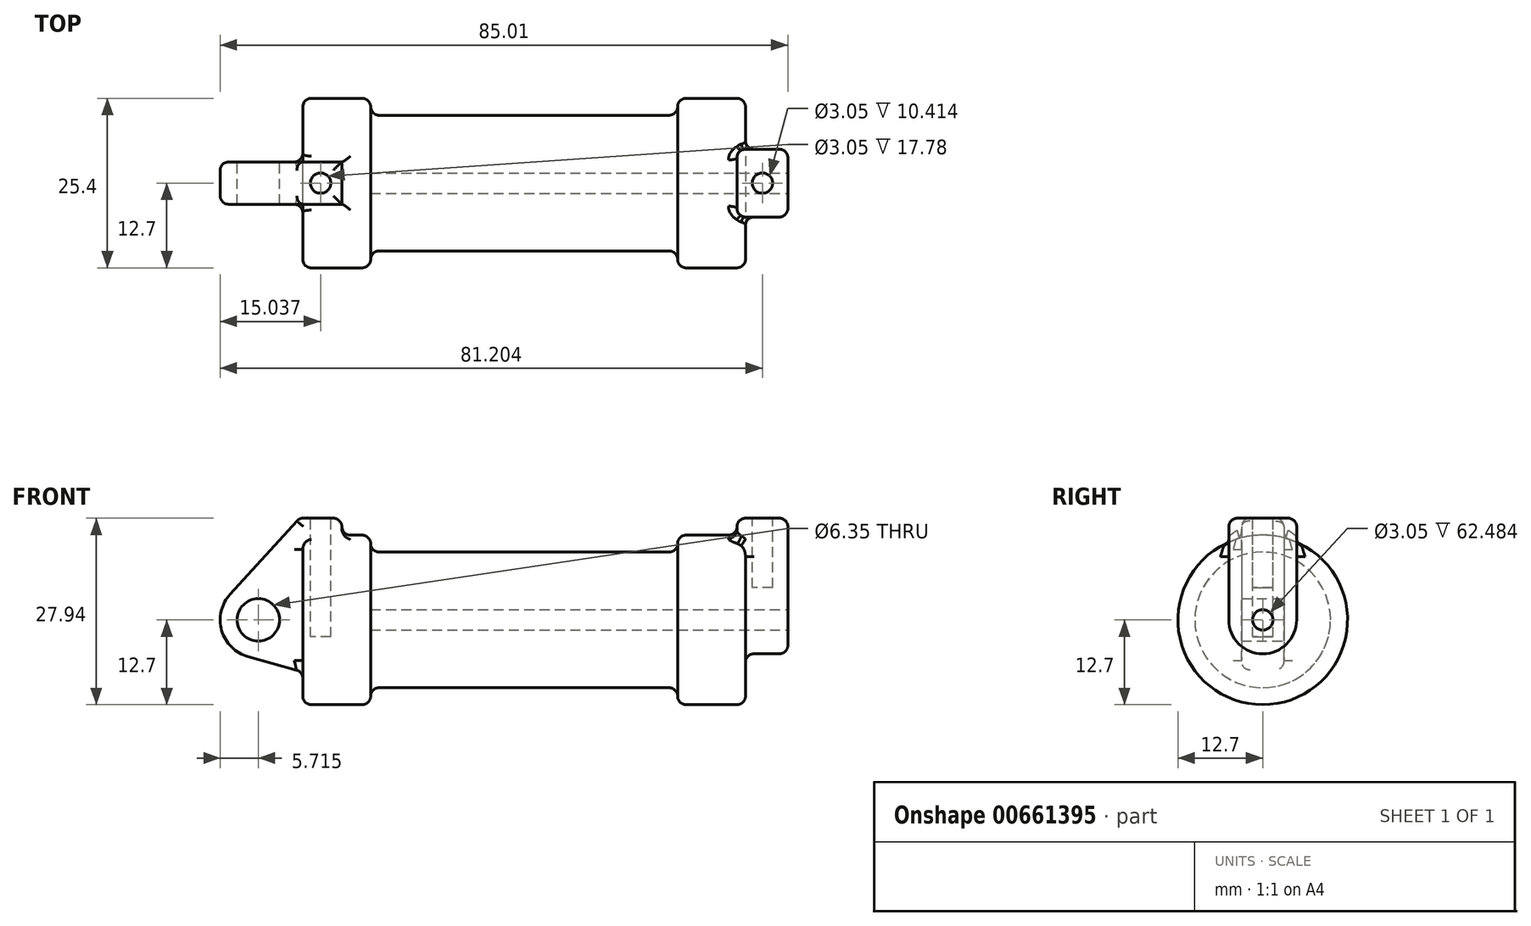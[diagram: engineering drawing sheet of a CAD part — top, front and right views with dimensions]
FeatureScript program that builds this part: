
annotation { "Feature Type Name" : "Feature", "Feature Type Description" : "" }
export const myFeature = defineFeature(function(context is Context, id is Id, definition is map)
    precondition{}
    {
        {
            var Q0;
            Q0=qCreatedBy(makeId("Front.planeOp"),FACE);
            var sketch = newSketch(context, id + "F0", { "sketchPlane" : qUnion([Q0])});
            skLineSegment(sketch, "E0", {"start": v(0, 0) * mm, "end": v(0, 12.7) * mm});
            skLineSegment(sketch, "E1", {"start": v(0, 12.7) * mm, "end": v(10.16, 12.7) * mm});
            skLineSegment(sketch, "E2", {"start": v(10.16, 12.7) * mm, "end": v(10.16, 10.16) * mm});
            skLineSegment(sketch, "E3", {"start": v(10.16, 10.16) * mm, "end": v(56.13, 10.16) * mm});
            skLineSegment(sketch, "E4", {"start": v(56.13, 10.16) * mm, "end": v(56.13, 12.7) * mm});
            skLineSegment(sketch, "E5", {"start": v(56.13, 12.7) * mm, "end": v(66.3, 12.7) * mm});
            skLineSegment(sketch, "E6", {"start": v(66.3, 12.7) * mm, "end": v(66.3, 0) * mm});
            skLineSegment(sketch, "E7", {"start": v(66.3, 0) * mm, "end": v(0, 0) * mm});
            skLineSegment(sketch, "E8", {"start": v(5.84, 15.24) * mm, "end": v(-0.5, 15.24) * mm});
            skLineSegment(sketch, "E9", {"start": v(-0.5, 15.24) * mm, "end": v(-10.88, 3.85) * mm});
            skLineSegment(sketch, "E10", {"start": v(0, 0) * mm, "end": v(-6.65, 0) * mm});
            skCircle(sketch, "E11", {"center": v(-6.65, 0) * mm, "radius": 5.72 * mm});
            skCircle(sketch, "E12", {"center": v(-6.65, 0) * mm, "radius": 3.18 * mm});
            skLineSegment(sketch, "E13", {"start": v(5.84, 15.24) * mm, "end": v(5.84, -9.4) * mm});
            skLineSegment(sketch, "E14", {"start": v(5.84, -9.4) * mm, "end": v(-8.18, -5.5) * mm});
            skSolve(sketch);
        }
        {
            var Q0;
            {var subQ1=sQuery(id+"F0.wireOp",EDGE,"E0");Q0=makeQuery(id+"F0.imprint","IMPRINT",FACE,{"disambiguationData":[TD([[makeQuery(id+"F0.imprint","IMPRINT",EDGE,{"derivedFrom":subQ1}),1.0]])]});}
            var Q1;
            {var subQ0=sQuery(id+"F0.wireOp",EDGE,"E14");Q1=makeQuery(id+"F0.imprint","IMPRINT",FACE,{"disambiguationData":[TD([[makeQuery(id+"F0.imprint","IMPRINT",EDGE,{"derivedFrom":subQ0}),-1.0]])]});}
            var Q2;
            {var subQ5=sQuery(id+"F0.wireOp",EDGE,"E12");Q2=makeQuery(id+"F0.imprint","IMPRINT",FACE,{"disambiguationData":[TD([[makeQuery(id+"F0.imprint","IMPRINT",EDGE,{"derivedFrom":subQ5}),-1.0]])]});}
            extrude(context, id + "F1", {"entities" : qUnion([Q0, Q1, Q2]), "endBound" : BoundingType.SYMMETRIC, "depth" : 6.35 * mm, "offsetDistance" : 25.4 * mm});
        }
        {
            var Q0;
            {var subQ0=sQuery(id+"F0.wireOp",EDGE,"E0");Q0=makeQuery(id+"F0.imprint","IMPRINT",FACE,{"disambiguationData":[TD([[makeQuery(id+"F0.imprint","IMPRINT",EDGE,{"derivedFrom":subQ0}),-1.0]])]});}
            var Q1;
            {var subQ0=sQuery(id+"F0.wireOp",EDGE,"E2");Q1=makeQuery(id+"F0.imprint","IMPRINT",FACE,{"disambiguationData":[TD([[makeQuery(id+"F0.imprint","IMPRINT",EDGE,{"derivedFrom":subQ0}),-1.0]])]});}
            var Q2;
            Q2=sQuery(id+"F0.wireOp",EDGE,"E7");
            revolve(context, id + "F2", {"operationType" : NewBodyOperationType.INTERSECT, "entities" : qUnion([Q0, Q1]), "axis" : qUnion([Q2]), "revolveType" : RevolveType.FULL});
        }
        {
            var Q0;
            Q0=makeQuery(id+"F1.opExtrude","SWEPT_BODY",BODY,{"disambiguationData":[OSD([sQuery(id+"F0.wireOp",EDGE,"E0"),sQuery(id+"F0.wireOp",EDGE,"E1"),sQuery(id+"F0.wireOp",EDGE,"E7"),sQuery(id+"F0.wireOp",EDGE,"E8"),sQuery(id+"F0.wireOp",EDGE,"E9"),sQuery(id+"F0.wireOp",EDGE,"E11"),sQuery(id+"F0.wireOp",EDGE,"E12"),sQuery(id+"F0.wireOp",EDGE,"E13"),sQuery(id+"F0.wireOp",EDGE,"E14")])]});
            deleteBodies(context, id + "F3", {"entities" : qUnion([Q0])});
        }
        {
            var Q0;
            {var subQ0=sQuery(id+"F0.wireOp",EDGE,"E2");Q0=makeQuery(id+"F0.imprint","IMPRINT",FACE,{"disambiguationData":[TD([[makeQuery(id+"F0.imprint","IMPRINT",EDGE,{"derivedFrom":subQ0}),-1.0]])]});}
            var Q1;
            {var subQ0=sQuery(id+"F0.wireOp",EDGE,"E0");Q1=makeQuery(id+"F0.imprint","IMPRINT",FACE,{"disambiguationData":[TD([[makeQuery(id+"F0.imprint","IMPRINT",EDGE,{"derivedFrom":subQ0}),-1.0]])]});}
            var Q2;
            Q2=sQuery(id+"F0.wireOp",EDGE,"E7");
            revolve(context, id + "F4", {"entities" : qUnion([Q0, Q1]), "axis" : qUnion([Q2]), "revolveType" : RevolveType.FULL});
        }
        {
            var Q0;
            {var subQ0=sQuery(id+"F0.wireOp",EDGE,"E0");Q0=makeQuery(id+"F0.imprint","IMPRINT",FACE,{"disambiguationData":[TD([[makeQuery(id+"F0.imprint","IMPRINT",EDGE,{"derivedFrom":subQ0}),-1.0]])]});}
            var Q1;
            {var subQ0=sQuery(id+"F0.wireOp",EDGE,"E14");Q1=makeQuery(id+"F0.imprint","IMPRINT",FACE,{"disambiguationData":[TD([[makeQuery(id+"F0.imprint","IMPRINT",EDGE,{"derivedFrom":subQ0}),-1.0]])]});}
            var Q2;
            {var subQ5=sQuery(id+"F0.wireOp",EDGE,"E12");Q2=makeQuery(id+"F0.imprint","IMPRINT",FACE,{"disambiguationData":[TD([[makeQuery(id+"F0.imprint","IMPRINT",EDGE,{"derivedFrom":subQ5}),-1.0]])]});}
            var Q3;
            {var subQ1=sQuery(id+"F0.wireOp",EDGE,"E0");Q3=makeQuery(id+"F0.imprint","IMPRINT",FACE,{"disambiguationData":[TD([[makeQuery(id+"F0.imprint","IMPRINT",EDGE,{"derivedFrom":subQ1}),1.0]])]});}
            extrude(context, id + "F5", {"entities" : qUnion([Q0, Q1, Q2, Q3]), "operationType" : NewBodyOperationType.ADD, "endBound" : BoundingType.SYMMETRIC, "depth" : 6.35 * mm, "offsetDistance" : 25.4 * mm});
        }
        {
            var Q0;
            Q0=makeQuery(id+"F4.opRevolve","SWEPT_FACE",FACE,{"disambiguationData":[OSD([sQuery(id+"F0.wireOp",EDGE,"E6")])]});
            var sketch = newSketch(context, id + "F6", { "sketchPlane" : qUnion([Q0])});
            skCircle(sketch, "E15", {"center": v(0, 0) * mm, "radius": 1.52 * mm});
            skCircle(sketch, "E16", {"center": v(0, 0) * mm, "radius": 5.08 * mm});
            skLineSegment(sketch, "E17", {"start": v(5.08, 0) * mm, "end": v(5.08, 15.24) * mm});
            skLineSegment(sketch, "E18", {"start": v(-5.08, 0) * mm, "end": v(-5.08, 15.24) * mm});
            skLineSegment(sketch, "E19", {"start": v(-5.08, 15.24) * mm, "end": v(5.08, 15.24) * mm});
            skSolve(sketch);
        }
        {
            var Q0;
            {var subQ0=sQuery(id+"F6.wireOp",EDGE,"E19");Q0=makeQuery(id+"F6.imprint","IMPRINT",FACE,{"disambiguationData":[TD([[makeQuery(id+"F6.imprint","IMPRINT",EDGE,{"derivedFrom":subQ0}),-1.0]])]});}
            var Q1;
            {var subQ0=sQuery(id+"F6.wireOp",EDGE,"E17");var subQ1=sQuery(id+"F6.wireOp",EDGE,"E16");var subQ2=makeQuery(id+"F6.imprint","INTERSECT",VERTEX,{"derivedFrom":[subQ1,subQ0]});Q1=makeQuery(id+"F6.imprint","IMPRINT",FACE,{"disambiguationData":[TD([[makeQuery(id+"F6.imprint","IMPRINT",EDGE,{"disambiguationData":[TD([[subQ2,-1.0]])],"derivedFrom":subQ1}),-1.0]])]});}
            var Q2;
            Q2=makeQuery(id+"F6.imprint","IMPRINT",FACE,{"disambiguationData":[TD([[makeQuery(id+"F6.imprint","IMPRINT",EDGE,{"derivedFrom":sQuery(id+"F6.wireOp",EDGE,"E15")}),-1.0]])]});
            extrude(context, id + "F7", {"entities" : qUnion([Q0, Q1, Q2]), "operationType" : NewBodyOperationType.ADD, "oppositeDirection" : true, "depth" : 1.27 * mm, "offsetDistance" : 25.4 * mm, "hasSecondDirection" : true, "secondDirectionOppositeDirection" : false, "secondDirectionDepth" : 6.35 * mm});
        }
        {
            var Q0;
            Q0=makeQuery(id+"F7.boolean.opBoolean","SPLIT",FACE,{"disambiguationData":[TD([makeQuery(id+"F7.opExtrude","SWEPT_FACE",FACE,{"disambiguationData":[OSD([sQuery(id+"F6.wireOp",EDGE,"E15")])]})])],"derivedFrom":makeQuery(id+"F4.opRevolve","SWEPT_FACE",FACE,{"disambiguationData":[OSD([sQuery(id+"F0.wireOp",EDGE,"E6")])]})});
            var Q1;
            Q1=makeQuery(id+"F4.opRevolve","SWEPT_FACE",FACE,{"disambiguationData":[OSD([sQuery(id+"F0.wireOp",EDGE,"E2")])]});
            extrude(context, id + "F8", {"entities" : qUnion([Q0]), "operationType" : NewBodyOperationType.REMOVE, "endBound" : BoundingType.UP_TO_SURFACE, "oppositeDirection" : true, "depth" : 25.4 * mm, "endBoundEntityFace" : qUnion([Q1]), "offsetDistance" : 25.4 * mm});
        }
        {
            var Q0;
            Q0=makeQuery(id+"F7.opExtrude","SWEPT_FACE",FACE,{"disambiguationData":[OSD([sQuery(id+"F6.wireOp",EDGE,"E19")])]});
            var sketch = newSketch(context, id + "F9", { "sketchPlane" : qUnion([Q0])});
            skCircle(sketch, "E20", {"center": v(68.83, 0) * mm, "radius": 1.52 * mm});
            skPoint(sketch, "E20.centerSnap0", {"position": v(68.83, 5.08) * mm});
            skPoint(sketch, "E20.centerSnap1", {"position": v(72.64, 0) * mm});
            skSolve(sketch);
        }
        {
            var Q0;
            Q0=makeQuery(id+"F9.imprint","IMPRINT",FACE,{"disambiguationData":[TD([[makeQuery(id+"F9.imprint","IMPRINT",EDGE,{"derivedFrom":sQuery(id+"F9.wireOp",EDGE,"E20")}),1.0]])]});
            extrude(context, id + "F10", {"entities" : qUnion([Q0]), "operationType" : NewBodyOperationType.REMOVE, "oppositeDirection" : true, "depth" : 10.4 * mm, "offsetDistance" : 25.4 * mm});
        }
        {
            var Q0;
            Q0=makeQuery(id+"F5.opExtrude","SWEPT_FACE",FACE,{"disambiguationData":[OSD([sQuery(id+"F0.wireOp",EDGE,"E8")])]});
            var sketch = newSketch(context, id + "F11", { "sketchPlane" : qUnion([Q0])});
            skCircle(sketch, "E21", {"center": v(2.67, 0) * mm, "radius": 1.52 * mm});
            skPoint(sketch, "E21.centerSnap0", {"position": v(5.84, 0) * mm});
            skPoint(sketch, "E21.centerSnap1", {"position": v(2.67, 3.18) * mm});
            skSolve(sketch);
        }
        {
            var Q0;
            Q0=makeQuery(id+"F11.imprint","IMPRINT",FACE,{"disambiguationData":[TD([[makeQuery(id+"F11.imprint","IMPRINT",EDGE,{"derivedFrom":sQuery(id+"F11.wireOp",EDGE,"E21")}),1.0]])]});
            extrude(context, id + "F12", {"entities" : qUnion([Q0]), "operationType" : NewBodyOperationType.REMOVE, "oppositeDirection" : true, "depth" : 17.78 * mm, "offsetDistance" : 25.4 * mm});
        }
        {
            var Q0;
            Q0=makeQuery(id+"F4.opRevolve","SWEPT_EDGE",EDGE,{"disambiguationData":[OSD([sQuery(id+"F0.wireOp",EDGE,"E0"),sQuery(id+"F0.wireOp",EDGE,"E1")])]});
            var Q1;
            Q1=makeQuery(id+"F4.opRevolve","SWEPT_EDGE",EDGE,{"disambiguationData":[OSD([sQuery(id+"F0.wireOp",EDGE,"E1"),sQuery(id+"F0.wireOp",EDGE,"E2")])]});
            var Q2;
            Q2=makeQuery(id+"F4.opRevolve","SWEPT_EDGE",EDGE,{"disambiguationData":[OSD([sQuery(id+"F0.wireOp",EDGE,"E4"),sQuery(id+"F0.wireOp",EDGE,"E5")])]});
            var Q3;
            Q3=makeQuery(id+"F4.opRevolve","SWEPT_EDGE",EDGE,{"disambiguationData":[OSD([sQuery(id+"F0.wireOp",EDGE,"E5"),sQuery(id+"F0.wireOp",EDGE,"E6")])]});
            fillet(context, id + "F13", {"entities" : qUnion([Q0, Q1, Q2, Q3]), "radius" : 1.27 * mm, "tangentPropagation" : true, "allowEdgeOverflow" : false});
        }
        {
            var Q0;
            Q0=makeQuery(id+"F7.opExtrude","CAP_EDGE",EDGE,{"disambiguationData":[OSD([sQuery(id+"F6.wireOp",EDGE,"E17")])],"isStart":true});
            var Q1;
            Q1=makeQuery(id+"F7.opExtrude","CAP_EDGE",EDGE,{"disambiguationData":[OSD([sQuery(id+"F6.wireOp",EDGE,"E19")])],"isStart":true});
            var Q2;
            Q2=makeQuery(id+"F7.opExtrude","SWEPT_EDGE",EDGE,{"disambiguationData":[OSD([sQuery(id+"F6.wireOp",EDGE,"E18"),sQuery(id+"F6.wireOp",EDGE,"E19")])]});
            var Q3;
            Q3=makeQuery(id+"F7.opExtrude","CAP_EDGE",EDGE,{"disambiguationData":[OSD([sQuery(id+"F6.wireOp",EDGE,"E19")])],"isStart":false});
            var Q4;
            Q4=makeQuery(id+"F7.opExtrude","SWEPT_EDGE",EDGE,{"disambiguationData":[OSD([sQuery(id+"F6.wireOp",EDGE,"E17"),sQuery(id+"F6.wireOp",EDGE,"E19")])]});
            var Q5;
            Q5=makeQuery(id+"F7.opExtrude","CAP_EDGE",EDGE,{"disambiguationData":[OSD([sQuery(id+"F6.wireOp",EDGE,"E17")])],"isStart":false});
            var Q6;
            Q6=makeQuery(id+"F13.opFillet","BLEND_EDGE",EDGE,{"blendedFrom":[makeQuery(id+"F4.opRevolve","SWEPT_EDGE",EDGE,{"disambiguationData":[OSD([sQuery(id+"F0.wireOp",EDGE,"E5"),sQuery(id+"F0.wireOp",EDGE,"E6")])]}),makeQuery(id+"F7.opExtrude","SWEPT_FACE",FACE,{"disambiguationData":[OSD([sQuery(id+"F6.wireOp",EDGE,"E17")])]})],"blendedInto":[makeQuery(id+"F7.opExtrude","SWEPT_FACE",FACE,{"disambiguationData":[OSD([sQuery(id+"F6.wireOp",EDGE,"E17")])]})]});
            var Q7;
            Q7=makeQuery(id+"F7.boolean.opBoolean","INTERSECT",EDGE,{"derivedFrom":[makeQuery(id+"F4.opRevolve","SWEPT_FACE",FACE,{"disambiguationData":[OSD([sQuery(id+"F0.wireOp",EDGE,"E6")])]}),makeQuery(id+"F7.opExtrude","SWEPT_FACE",FACE,{"disambiguationData":[OSD([sQuery(id+"F6.wireOp",EDGE,"E17")])]})]});
            var Q8;
            Q8=makeQuery(id+"F7.opExtrude","CAP_EDGE",EDGE,{"disambiguationData":[OSD([sQuery(id+"F6.wireOp",EDGE,"E16")])],"isStart":true});
            var Q9;
            Q9=makeQuery(id+"F7.opExtrude","CAP_EDGE",EDGE,{"disambiguationData":[OSD([sQuery(id+"F6.wireOp",EDGE,"E18")])],"isStart":true});
            var Q10;
            Q10=makeQuery(id+"F7.boolean.opBoolean","INTERSECT",EDGE,{"derivedFrom":[makeQuery(id+"F4.opRevolve","SWEPT_FACE",FACE,{"disambiguationData":[OSD([sQuery(id+"F0.wireOp",EDGE,"E6")])]}),makeQuery(id+"F7.opExtrude","SWEPT_FACE",FACE,{"disambiguationData":[OSD([sQuery(id+"F6.wireOp",EDGE,"E16")])]})]});
            var Q11;
            Q11=makeQuery(id+"F7.boolean.opBoolean","INTERSECT",EDGE,{"derivedFrom":[makeQuery(id+"F4.opRevolve","SWEPT_FACE",FACE,{"disambiguationData":[OSD([sQuery(id+"F0.wireOp",EDGE,"E6")])]}),makeQuery(id+"F7.opExtrude","SWEPT_FACE",FACE,{"disambiguationData":[OSD([sQuery(id+"F6.wireOp",EDGE,"E18")])]})]});
            var Q12;
            Q12=makeQuery(id+"F13.opFillet","BLEND_EDGE",EDGE,{"blendedFrom":[makeQuery(id+"F4.opRevolve","SWEPT_EDGE",EDGE,{"disambiguationData":[OSD([sQuery(id+"F0.wireOp",EDGE,"E5"),sQuery(id+"F0.wireOp",EDGE,"E6")])]}),makeQuery(id+"F7.opExtrude","SWEPT_FACE",FACE,{"disambiguationData":[OSD([sQuery(id+"F6.wireOp",EDGE,"E18")])]})],"blendedInto":[makeQuery(id+"F7.opExtrude","SWEPT_FACE",FACE,{"disambiguationData":[OSD([sQuery(id+"F6.wireOp",EDGE,"E18")])]})]});
            var Q13;
            Q13=makeQuery(id+"F7.opExtrude","CAP_EDGE",EDGE,{"disambiguationData":[OSD([sQuery(id+"F6.wireOp",EDGE,"E18")])],"isStart":false});
            var Q14;
            Q14=makeQuery(id+"F7.boolean.opBoolean","INTERSECT",EDGE,{"derivedFrom":[makeQuery(id+"F4.opRevolve","SWEPT_FACE",FACE,{"disambiguationData":[OSD([sQuery(id+"F0.wireOp",EDGE,"E5")])]}),makeQuery(id+"F7.opExtrude","CAP_FACE",FACE,{"disambiguationData":[OSD([sQuery(id+"F6.wireOp",EDGE,"E15"),sQuery(id+"F6.wireOp",EDGE,"E16"),sQuery(id+"F6.wireOp",EDGE,"E17"),sQuery(id+"F6.wireOp",EDGE,"E18"),sQuery(id+"F6.wireOp",EDGE,"E19")])],"isStart":false})]});
            fillet(context, id + "F14", {"entities" : qUnion([Q0, Q1, Q2, Q3, Q4, Q5, Q6, Q7, Q8, Q9, Q10, Q11, Q12, Q13, Q14]), "radius" : 1.27 * mm, "tangentPropagation" : true, "allowEdgeOverflow" : false});
        }
        {
            var Q0;
            Q0=makeQuery(id+"F5.opExtrude","CAP_EDGE",EDGE,{"disambiguationData":[OSD([sQuery(id+"F0.wireOp",EDGE,"E8")])],"isStart":false});
            var Q1;
            Q1=makeQuery(id+"F5.opExtrude","SWEPT_EDGE",EDGE,{"disambiguationData":[OSD([sQuery(id+"F0.wireOp",EDGE,"E8"),sQuery(id+"F0.wireOp",EDGE,"E13")])]});
            var Q2;
            Q2=makeQuery(id+"F5.opExtrude","CAP_EDGE",EDGE,{"disambiguationData":[OSD([sQuery(id+"F0.wireOp",EDGE,"E8")])],"isStart":true});
            var Q3;
            Q3=makeQuery(id+"F5.boolean.opBoolean","INTERSECT",EDGE,{"derivedFrom":[makeQuery(id+"F4.opRevolve","SWEPT_FACE",FACE,{"disambiguationData":[OSD([sQuery(id+"F0.wireOp",EDGE,"E1")])]}),makeQuery(id+"F5.opExtrude","SWEPT_FACE",FACE,{"disambiguationData":[OSD([sQuery(id+"F0.wireOp",EDGE,"E13")])]})]});
            var Q4;
            Q4=makeQuery(id+"F5.boolean.opBoolean","INTERSECT",EDGE,{"derivedFrom":[makeQuery(id+"F4.opRevolve","SWEPT_FACE",FACE,{"disambiguationData":[OSD([sQuery(id+"F0.wireOp",EDGE,"E1")])]}),makeQuery(id+"F5.opExtrude","CAP_FACE",FACE,{"disambiguationData":[OSD([sQuery(id+"F0.wireOp",EDGE,"E8"),sQuery(id+"F0.wireOp",EDGE,"E9"),sQuery(id+"F0.wireOp",EDGE,"E11"),sQuery(id+"F0.wireOp",EDGE,"E12"),sQuery(id+"F0.wireOp",EDGE,"E13"),sQuery(id+"F0.wireOp",EDGE,"E14")])],"isStart":false})]});
            var Q5;
            Q5=makeQuery(id+"F5.boolean.opBoolean","INTERSECT",EDGE,{"derivedFrom":[makeQuery(id+"F4.opRevolve","SWEPT_FACE",FACE,{"disambiguationData":[OSD([sQuery(id+"F0.wireOp",EDGE,"E1")])]}),makeQuery(id+"F5.opExtrude","CAP_FACE",FACE,{"disambiguationData":[OSD([sQuery(id+"F0.wireOp",EDGE,"E8"),sQuery(id+"F0.wireOp",EDGE,"E9"),sQuery(id+"F0.wireOp",EDGE,"E11"),sQuery(id+"F0.wireOp",EDGE,"E12"),sQuery(id+"F0.wireOp",EDGE,"E13"),sQuery(id+"F0.wireOp",EDGE,"E14")])],"isStart":true})]});
            var Q6;
            Q6=makeQuery(id+"F13.opFillet","BLEND_EDGE",EDGE,{"blendedFrom":[makeQuery(id+"F4.opRevolve","SWEPT_EDGE",EDGE,{"disambiguationData":[OSD([sQuery(id+"F0.wireOp",EDGE,"E0"),sQuery(id+"F0.wireOp",EDGE,"E1")])]}),makeQuery(id+"F5.opExtrude","CAP_FACE",FACE,{"disambiguationData":[OSD([sQuery(id+"F0.wireOp",EDGE,"E8"),sQuery(id+"F0.wireOp",EDGE,"E9"),sQuery(id+"F0.wireOp",EDGE,"E11"),sQuery(id+"F0.wireOp",EDGE,"E12"),sQuery(id+"F0.wireOp",EDGE,"E13"),sQuery(id+"F0.wireOp",EDGE,"E14")])],"isStart":true})],"blendedInto":[makeQuery(id+"F5.opExtrude","CAP_FACE",FACE,{"disambiguationData":[OSD([sQuery(id+"F0.wireOp",EDGE,"E8"),sQuery(id+"F0.wireOp",EDGE,"E9"),sQuery(id+"F0.wireOp",EDGE,"E11"),sQuery(id+"F0.wireOp",EDGE,"E12"),sQuery(id+"F0.wireOp",EDGE,"E13"),sQuery(id+"F0.wireOp",EDGE,"E14")])],"isStart":true})]});
            var Q7;
            Q7=makeQuery(id+"F5.boolean.opBoolean","INTERSECT",EDGE,{"derivedFrom":[makeQuery(id+"F4.opRevolve","SWEPT_FACE",FACE,{"disambiguationData":[OSD([sQuery(id+"F0.wireOp",EDGE,"E0")])]}),makeQuery(id+"F5.opExtrude","CAP_FACE",FACE,{"disambiguationData":[OSD([sQuery(id+"F0.wireOp",EDGE,"E8"),sQuery(id+"F0.wireOp",EDGE,"E9"),sQuery(id+"F0.wireOp",EDGE,"E11"),sQuery(id+"F0.wireOp",EDGE,"E12"),sQuery(id+"F0.wireOp",EDGE,"E13"),sQuery(id+"F0.wireOp",EDGE,"E14")])],"isStart":true})]});
            var Q8;
            Q8=makeQuery(id+"F5.opExtrude","CAP_EDGE",EDGE,{"disambiguationData":[OSD([sQuery(id+"F0.wireOp",EDGE,"E9")])],"isStart":true});
            var Q9;
            Q9=makeQuery(id+"F5.opExtrude","CAP_EDGE",EDGE,{"disambiguationData":[OSD([sQuery(id+"F0.wireOp",EDGE,"E9")])],"isStart":false});
            var Q10;
            Q10=makeQuery(id+"F13.opFillet","BLEND_EDGE",EDGE,{"blendedFrom":[makeQuery(id+"F4.opRevolve","SWEPT_EDGE",EDGE,{"disambiguationData":[OSD([sQuery(id+"F0.wireOp",EDGE,"E0"),sQuery(id+"F0.wireOp",EDGE,"E1")])]}),makeQuery(id+"F5.opExtrude","CAP_FACE",FACE,{"disambiguationData":[OSD([sQuery(id+"F0.wireOp",EDGE,"E8"),sQuery(id+"F0.wireOp",EDGE,"E9"),sQuery(id+"F0.wireOp",EDGE,"E11"),sQuery(id+"F0.wireOp",EDGE,"E12"),sQuery(id+"F0.wireOp",EDGE,"E13"),sQuery(id+"F0.wireOp",EDGE,"E14")])],"isStart":false})],"blendedInto":[makeQuery(id+"F5.opExtrude","CAP_FACE",FACE,{"disambiguationData":[OSD([sQuery(id+"F0.wireOp",EDGE,"E8"),sQuery(id+"F0.wireOp",EDGE,"E9"),sQuery(id+"F0.wireOp",EDGE,"E11"),sQuery(id+"F0.wireOp",EDGE,"E12"),sQuery(id+"F0.wireOp",EDGE,"E13"),sQuery(id+"F0.wireOp",EDGE,"E14")])],"isStart":false})]});
            var Q11;
            Q11=makeQuery(id+"F5.boolean.opBoolean","INTERSECT",EDGE,{"derivedFrom":[makeQuery(id+"F4.opRevolve","SWEPT_FACE",FACE,{"disambiguationData":[OSD([sQuery(id+"F0.wireOp",EDGE,"E0")])]}),makeQuery(id+"F5.opExtrude","CAP_FACE",FACE,{"disambiguationData":[OSD([sQuery(id+"F0.wireOp",EDGE,"E8"),sQuery(id+"F0.wireOp",EDGE,"E9"),sQuery(id+"F0.wireOp",EDGE,"E11"),sQuery(id+"F0.wireOp",EDGE,"E12"),sQuery(id+"F0.wireOp",EDGE,"E13"),sQuery(id+"F0.wireOp",EDGE,"E14")])],"isStart":false})]});
            var Q12;
            Q12=makeQuery(id+"F5.boolean.opBoolean","INTERSECT",EDGE,{"derivedFrom":[makeQuery(id+"F4.opRevolve","SWEPT_FACE",FACE,{"disambiguationData":[OSD([sQuery(id+"F0.wireOp",EDGE,"E0")])]}),makeQuery(id+"F5.opExtrude","SWEPT_FACE",FACE,{"disambiguationData":[OSD([sQuery(id+"F0.wireOp",EDGE,"E14")])]})]});
            var Q13;
            Q13=makeQuery(id+"F5.opExtrude","CAP_EDGE",EDGE,{"disambiguationData":[OSD([sQuery(id+"F0.wireOp",EDGE,"E11")])],"isStart":false});
            var Q14;
            Q14=makeQuery(id+"F5.opExtrude","CAP_EDGE",EDGE,{"disambiguationData":[OSD([sQuery(id+"F0.wireOp",EDGE,"E14")])],"isStart":false});
            var Q15;
            Q15=makeQuery(id+"F5.opExtrude","CAP_EDGE",EDGE,{"disambiguationData":[OSD([sQuery(id+"F0.wireOp",EDGE,"E11")])],"isStart":true});
            var Q16;
            Q16=makeQuery(id+"F5.opExtrude","CAP_EDGE",EDGE,{"disambiguationData":[OSD([sQuery(id+"F0.wireOp",EDGE,"E14")])],"isStart":true});
            fillet(context, id + "F15", {"entities" : qUnion([Q0, Q1, Q2, Q3, Q4, Q5, Q6, Q7, Q8, Q9, Q10, Q11, Q12, Q13, Q14, Q15, Q16]), "radius" : 1.27 * mm, "tangentPropagation" : true, "allowEdgeOverflow" : false});
        }
        {
            var Q0;
            Q0=makeQuery(id+"F5.opExtrude","SWEPT_EDGE",EDGE,{"disambiguationData":[OSD([sQuery(id+"F0.wireOp",EDGE,"E8"),sQuery(id+"F0.wireOp",EDGE,"E9")])]});
            fillet(context, id + "F16", {"entities" : qUnion([Q0]), "radius" : 1.27 * mm, "tangentPropagation" : true, "allowEdgeOverflow" : false});
        }
        {
            var Q0;
            Q0=makeQuery(id+"F4.opRevolve","SWEPT_EDGE",EDGE,{"disambiguationData":[OSD([sQuery(id+"F0.wireOp",EDGE,"E3"),sQuery(id+"F0.wireOp",EDGE,"E4")])]});
            var Q1;
            Q1=makeQuery(id+"F4.opRevolve","SWEPT_EDGE",EDGE,{"disambiguationData":[OSD([sQuery(id+"F0.wireOp",EDGE,"E2"),sQuery(id+"F0.wireOp",EDGE,"E3")])]});
            fillet(context, id + "F17", {"entities" : qUnion([Q0, Q1]), "radius" : 1.27 * mm, "tangentPropagation" : true, "allowEdgeOverflow" : false});
        }
    });
